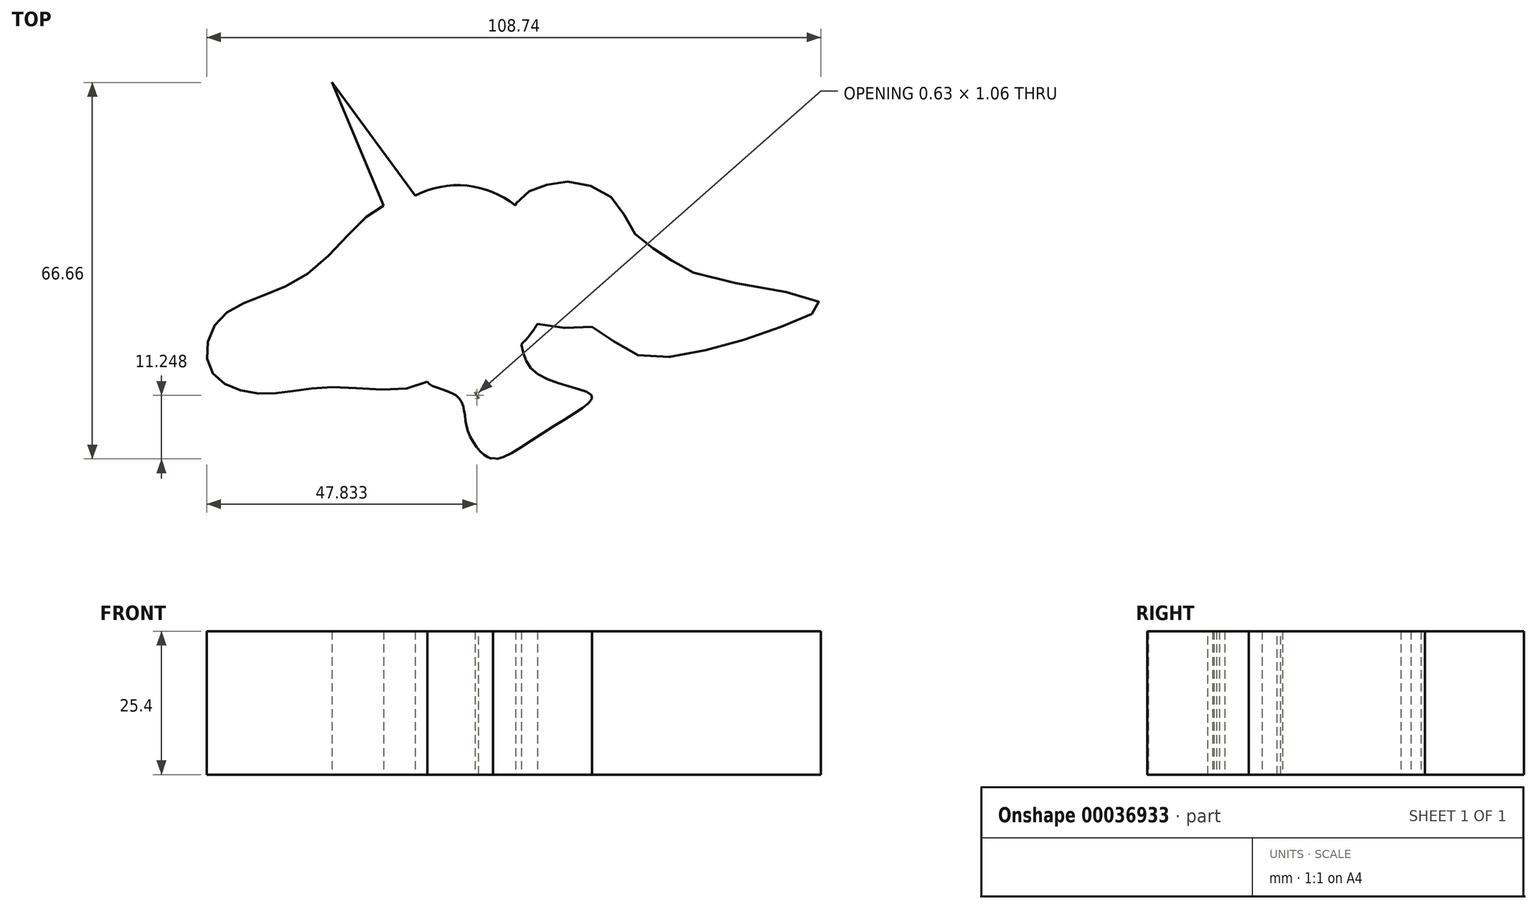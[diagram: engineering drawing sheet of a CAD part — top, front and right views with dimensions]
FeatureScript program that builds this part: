
annotation { "Feature Type Name" : "Feature", "Feature Type Description" : "" }
export const myFeature = defineFeature(function(context is Context, id is Id, definition is map)
    precondition{}
    {
        {
            var Q0;
            Q0=qCreatedBy(makeId("Top.planeOp"),FACE);
            var sketch = newSketch(context, id + "F0", { "sketchPlane" : qUnion([Q0])});
            skCircle(sketch, "E0", {"center": v(0, -12.74) * mm, "radius": 16.34 * mm});
            skCircle(sketch, "E1", {"center": v(-14.83, -19.59) * mm, "radius": 8 * mm});
            skFitSpline(sketch, "E2", {"points": [v(2, -25.3) * mm, v(3.7, -34.15) * mm, v(6.28, -39.57) * mm, v(6.28, -44.7) * mm, v(17.11, -39) * mm, v(23.67, -33.57) * mm, v(13.12, -29) * mm, v(9.98, -22.16) * mm, v(2, -25.3) * mm]});
            skFitSpline(sketch, "E3", {"points": [v(-10.23, 0) * mm, v(-25.96, -11.6) * mm, v(-41.93, -19.87) * mm, v(-43.64, -29.3) * mm, v(-34.51, -33.29) * mm, v(-21.4, -32.15) * mm, v(-3.07, -28.78) * mm, v(-10.23, 0) * mm]});
            skFitSpline(sketch, "E4", {"points": [v(10.23, 0) * mm, v(13.12, 2.68) * mm, v(17.4, 4.1) * mm, v(23.39, 3.53) * mm, v(28.52, 0) * mm, v(31.38, -5.03) * mm, v(36.51, -8.74) * mm, v(43.36, -12.45) * mm, v(64.18, -17.3) * mm, v(59.9, -20.44) * mm, v(42.79, -25.87) * mm, v(30.24, -25.87) * mm, v(23.1, -21.3) * mm, v(14.13, -20.94) * mm, v(10.23, 0) * mm]});
            skLineSegment(sketch, "E5", {"start": v(-7.53, 1.76) * mm, "end": v(-22.25, 21.8) * mm});
            skLineSegment(sketch, "E6", {"start": v(-22.25, 21.8) * mm, "end": v(-13.13, 0) * mm});
            skFitSpline(sketch, "E7", {"points": [v(-5.39, -31.19) * mm, v(0, -33.86) * mm, v(2, -40.43) * mm, v(6.28, -44.7) * mm, v(3.7, -34.15) * mm, v(-3.07, -28.78) * mm, v(-5.39, -31.19) * mm]});
            skCircle(sketch, "E8", {"center": v(18.26, -7.03) * mm, "radius": 10.8 * mm});
            skSolve(sketch);
        }
        {
            var Q0;
            {var subQ3=sQuery(id+"F0.wireOp",EDGE,"E0");var subQ14=makeQuery(id+"F0.imprint","INTERSECT",VERTEX,{"derivedFrom":[subQ3,sQuery(id+"F0.wireOp",EDGE,"E5")]});Q0=makeQuery(id+"F0.imprint","IMPRINT",FACE,{"disambiguationData":[TD([[makeQuery(id+"F0.imprint","IMPRINT",EDGE,{"disambiguationData":[TD([[subQ14,1.0]])],"derivedFrom":subQ3}),1.0]])]});}
            var Q1;
            {var subQ1=sQuery(id+"F0.wireOp",EDGE,"E5");Q1=makeQuery(id+"F0.imprint","IMPRINT",FACE,{"disambiguationData":[TD([[makeQuery(id+"F0.imprint","IMPRINT",EDGE,{"derivedFrom":subQ1}),1.0]])]});}
            var Q2;
            {var subQ0=sQuery(id+"F0.wireOp",EDGE,"E3");var subQ1=sQuery(id+"F0.wireOp",EDGE,"E0");var subQ3=makeQuery(id+"F0.imprint","INTERSECT",VERTEX,{"derivedFrom":[subQ1,subQ0]});Q2=makeQuery(id+"F0.imprint","IMPRINT",FACE,{"disambiguationData":[TD([[makeQuery(id+"F0.imprint","IMPRINT",EDGE,{"disambiguationData":[TD([[subQ3,-1.0]])],"derivedFrom":subQ1}),1.0]])]});}
            var Q3;
            {var subQ0=sQuery(id+"F0.wireOp",EDGE,"E1");var subQ1=sQuery(id+"F0.wireOp",EDGE,"E0");var subQ3=makeQuery(id+"F0.imprint","INTERSECT",VERTEX,{"disambiguationData":[OD(0.0)],"derivedFrom":[subQ1,subQ0]});Q3=makeQuery(id+"F0.imprint","IMPRINT",FACE,{"disambiguationData":[TD([[makeQuery(id+"F0.imprint","IMPRINT",EDGE,{"disambiguationData":[TD([[subQ3,-1.0]])],"derivedFrom":subQ1}),-1.0]])]});}
            var Q4;
            {var subQ0=sQuery(id+"F0.wireOp",EDGE,"E1");var subQ1=sQuery(id+"F0.wireOp",EDGE,"E0");var subQ3=makeQuery(id+"F0.imprint","INTERSECT",VERTEX,{"disambiguationData":[OD(0.0)],"derivedFrom":[subQ1,subQ0]});Q4=makeQuery(id+"F0.imprint","IMPRINT",FACE,{"disambiguationData":[TD([[makeQuery(id+"F0.imprint","IMPRINT",EDGE,{"disambiguationData":[TD([[subQ3,-1.0]])],"derivedFrom":subQ1}),1.0]])]});}
            var Q5;
            {var subQ0=sQuery(id+"F0.wireOp",EDGE,"E8");var subQ3=sQuery(id+"F0.wireOp",EDGE,"E0");var subQ4=makeQuery(id+"F0.imprint","INTERSECT",VERTEX,{"disambiguationData":[OD(0.0)],"derivedFrom":[subQ3,subQ0]});Q5=makeQuery(id+"F0.imprint","IMPRINT",FACE,{"disambiguationData":[TD([[makeQuery(id+"F0.imprint","IMPRINT",EDGE,{"disambiguationData":[TD([[subQ4,1.0]])],"derivedFrom":subQ3}),1.0]])]});}
            var Q6;
            {var subQ1=sQuery(id+"F0.wireOp",EDGE,"E4");var subQ3=sQuery(id+"F0.wireOp",EDGE,"E0");var subQ5=makeQuery(id+"F0.imprint","INTERSECT",VERTEX,{"disambiguationData":[OD(1.0)],"derivedFrom":[subQ3,subQ1]});Q6=makeQuery(id+"F0.imprint","IMPRINT",FACE,{"disambiguationData":[TD([[makeQuery(id+"F0.imprint","IMPRINT",EDGE,{"disambiguationData":[TD([[subQ5,1.0]])],"derivedFrom":subQ3}),1.0]])]});}
            var Q7;
            {var subQ1=sQuery(id+"F0.wireOp",EDGE,"E0");var subQ3=sQuery(id+"F0.wireOp",EDGE,"E4");var subQ5=makeQuery(id+"F0.imprint","INTERSECT",VERTEX,{"disambiguationData":[OD(0.0)],"derivedFrom":[subQ1,subQ3]});Q7=makeQuery(id+"F0.imprint","IMPRINT",FACE,{"disambiguationData":[TD([[makeQuery(id+"F0.imprint","IMPRINT",EDGE,{"disambiguationData":[TD([[subQ5,-1.0]])],"derivedFrom":subQ1}),-1.0]])]});}
            var Q8;
            {var subQ0=sQuery(id+"F0.wireOp",EDGE,"E2");var subQ1=sQuery(id+"F0.wireOp",EDGE,"E0");var subQ3=makeQuery(id+"F0.imprint","INTERSECT",VERTEX,{"disambiguationData":[OD(0.0)],"derivedFrom":[subQ1,subQ0]});Q8=makeQuery(id+"F0.imprint","IMPRINT",FACE,{"disambiguationData":[TD([[makeQuery(id+"F0.imprint","IMPRINT",EDGE,{"disambiguationData":[TD([[subQ3,1.0]])],"derivedFrom":subQ1}),1.0]])]});}
            var Q9;
            {var subQ1=sQuery(id+"F0.wireOp",EDGE,"E0");var subQ2=sQuery(id+"F0.wireOp",EDGE,"E3");var subQ6=makeQuery(id+"F0.imprint","INTERSECT",VERTEX,{"derivedFrom":[subQ1,subQ2]});Q9=makeQuery(id+"F0.imprint","IMPRINT",FACE,{"disambiguationData":[TD([[makeQuery(id+"F0.imprint","IMPRINT",EDGE,{"disambiguationData":[TD([[subQ6,-1.0]])],"derivedFrom":subQ1}),-1.0]])]});}
            var Q10;
            {var subQ1=sQuery(id+"F0.wireOp",EDGE,"E2");var subQ6=sQuery(id+"F0.wireOp",EDGE,"E0");var subQ7=makeQuery(id+"F0.imprint","INTERSECT",VERTEX,{"disambiguationData":[OD(0.0)],"derivedFrom":[subQ6,subQ1]});Q10=makeQuery(id+"F0.imprint","IMPRINT",FACE,{"disambiguationData":[TD([[makeQuery(id+"F0.imprint","IMPRINT",EDGE,{"disambiguationData":[TD([[subQ7,1.0]])],"derivedFrom":subQ6}),-1.0]])]});}
            var Q11;
            {var subQ0=sQuery(id+"F0.wireOp",EDGE,"E7");var subQ1=sQuery(id+"F0.wireOp",EDGE,"E2");var subQ2=makeQuery(id+"F0.imprint","INTERSECT",VERTEX,{"disambiguationData":[OD(1.0)],"derivedFrom":[subQ1,subQ0]});Q11=makeQuery(id+"F0.imprint","IMPRINT",FACE,{"disambiguationData":[TD([[makeQuery(id+"F0.imprint","IMPRINT",EDGE,{"disambiguationData":[TD([[subQ2,-1.0]])],"derivedFrom":subQ1}),-1.0]])]});}
            var Q12;
            {var subQ1=sQuery(id+"F0.wireOp",EDGE,"E0");var subQ3=sQuery(id+"F0.wireOp",EDGE,"E4");var subQ5=makeQuery(id+"F0.imprint","INTERSECT",VERTEX,{"disambiguationData":[OD(1.0)],"derivedFrom":[subQ1,subQ3]});Q12=makeQuery(id+"F0.imprint","IMPRINT",FACE,{"disambiguationData":[TD([[makeQuery(id+"F0.imprint","IMPRINT",EDGE,{"disambiguationData":[TD([[subQ5,1.0]])],"derivedFrom":subQ1}),-1.0]])]});}
            var Q13;
            {var subQ0=sQuery(id+"F0.wireOp",EDGE,"E7");var subQ1=sQuery(id+"F0.wireOp",EDGE,"E2");var subQ3=makeQuery(id+"F0.imprint","INTERSECT",VERTEX,{"disambiguationData":[OD(0.0)],"derivedFrom":[subQ1,subQ0]});Q13=makeQuery(id+"F0.imprint","IMPRINT",FACE,{"disambiguationData":[TD([[makeQuery(id+"F0.imprint","IMPRINT",EDGE,{"disambiguationData":[TD([[subQ3,1.0]])],"derivedFrom":subQ1}),1.0]])]});}
            var Q14;
            {var subQ0=sQuery(id+"F0.wireOp",EDGE,"E7");var subQ1=sQuery(id+"F0.wireOp",EDGE,"E3");var subQ3=makeQuery(id+"F0.imprint","INTERSECT",VERTEX,{"derivedFrom":[subQ1,subQ0]});Q14=makeQuery(id+"F0.imprint","IMPRINT",FACE,{"disambiguationData":[TD([[makeQuery(id+"F0.imprint","IMPRINT",EDGE,{"disambiguationData":[TD([[subQ3,-1.0]])],"derivedFrom":subQ1}),1.0]])]});}
            var Q15;
            {var subQ0=sQuery(id+"F0.wireOp",EDGE,"E7");var subQ3=sQuery(id+"F0.wireOp",EDGE,"E0");var subQ4=makeQuery(id+"F0.imprint","INTERSECT",VERTEX,{"derivedFrom":[subQ3,subQ0]});Q15=makeQuery(id+"F0.imprint","IMPRINT",FACE,{"disambiguationData":[TD([[makeQuery(id+"F0.imprint","IMPRINT",EDGE,{"disambiguationData":[TD([[subQ4,-1.0]])],"derivedFrom":subQ3}),-1.0]])]});}
            var Q16;
            {var subQ1=sQuery(id+"F0.wireOp",EDGE,"E4");var subQ3=sQuery(id+"F0.wireOp",EDGE,"E0");var subQ5=makeQuery(id+"F0.imprint","INTERSECT",VERTEX,{"disambiguationData":[OD(0.0)],"derivedFrom":[subQ3,subQ1]});Q16=makeQuery(id+"F0.imprint","IMPRINT",FACE,{"disambiguationData":[TD([[makeQuery(id+"F0.imprint","IMPRINT",EDGE,{"disambiguationData":[TD([[subQ5,-1.0]])],"derivedFrom":subQ3}),1.0]])]});}
            var Q17;
            {var subQ0=sQuery(id+"F0.wireOp",EDGE,"E7");var subQ1=sQuery(id+"F0.wireOp",EDGE,"E2");var subQ3=makeQuery(id+"F0.imprint","INTERSECT",VERTEX,{"disambiguationData":[OD(2.0)],"derivedFrom":[subQ1,subQ0]});Q17=makeQuery(id+"F0.imprint","IMPRINT",FACE,{"disambiguationData":[TD([[makeQuery(id+"F0.imprint","IMPRINT",EDGE,{"disambiguationData":[TD([[subQ3,-1.0]])],"derivedFrom":subQ1}),-1.0]])]});}
            var Q18;
            {var subQ0=sQuery(id+"F0.wireOp",EDGE,"E7");var subQ1=sQuery(id+"F0.wireOp",EDGE,"E0");var subQ3=makeQuery(id+"F0.imprint","INTERSECT",VERTEX,{"derivedFrom":[subQ1,subQ0]});Q18=makeQuery(id+"F0.imprint","IMPRINT",FACE,{"disambiguationData":[TD([[makeQuery(id+"F0.imprint","IMPRINT",EDGE,{"disambiguationData":[TD([[subQ3,1.0]])],"derivedFrom":subQ1}),1.0]])]});}
            extrude(context, id + "F1", {"entities" : qUnion([Q0, Q1, Q2, Q3, Q4, Q5, Q6, Q7, Q8, Q9, Q10, Q11, Q12, Q13, Q14, Q15, Q16, Q17, Q18]), "depth" : 25.4 * mm});
        }
    });
